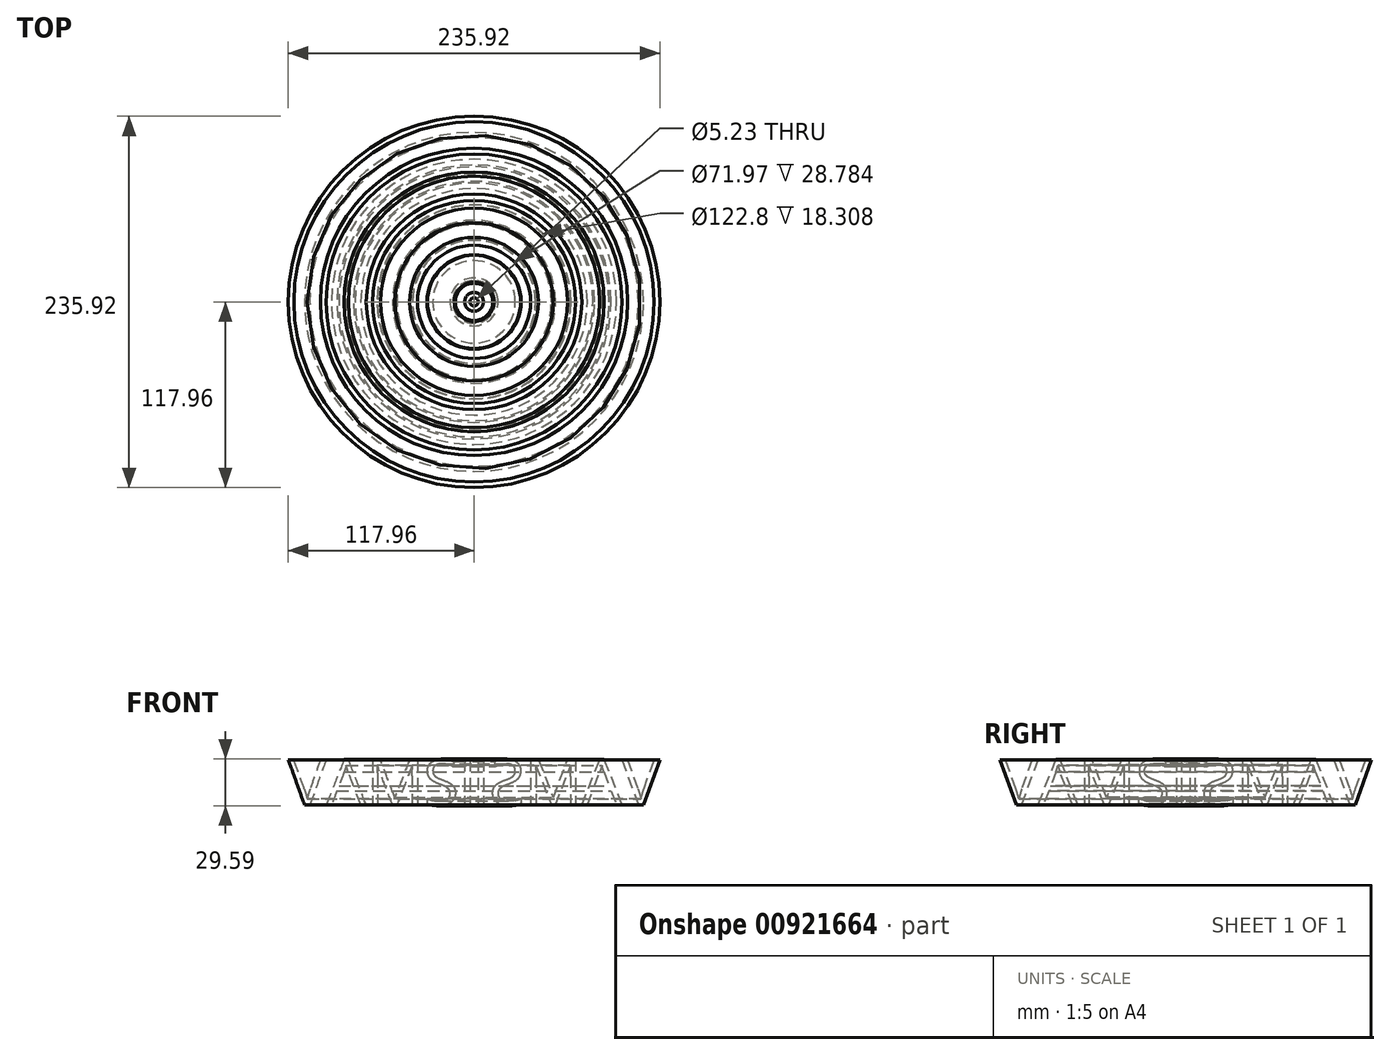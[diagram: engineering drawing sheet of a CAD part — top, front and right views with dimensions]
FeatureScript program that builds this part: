
annotation { "Feature Type Name" : "Feature", "Feature Type Description" : "" }
export const myFeature = defineFeature(function(context is Context, id is Id, definition is map)
    precondition{}
    {
        {
            var Q0;
            Q0=qCreatedBy(makeId("Front.planeOp"),FACE);
            var sketch = newSketch(context, id + "F0", { "sketchPlane" : qUnion([Q0])});
            skText(sketch, "E0", { "text": "VAMSI", "fontName": "OpenSans-Regular.ttf"});
            const initialGuessF0  = {"E0": [-0.1159, 0.01578, 1, 0, 0.02903]};
            skSetInitialGuess(sketch, initialGuessF0);
            skSolve(sketch);
        }
        {
            var Q0;
            Q0 = qSketchRegion(id + "F0", true);
            var Q1;
            Q1=sQuery(id+"F0.wireOp",EDGE,"E0.sketch_text.right");
            revolve(context, id + "F1", {"surfaceOperationType" : NewSurfaceOperationType.NEW, "entities" : qUnion([Q0]), "axis" : qUnion([Q1]), "revolveType" : RevolveType.FULL});
        }
    });
